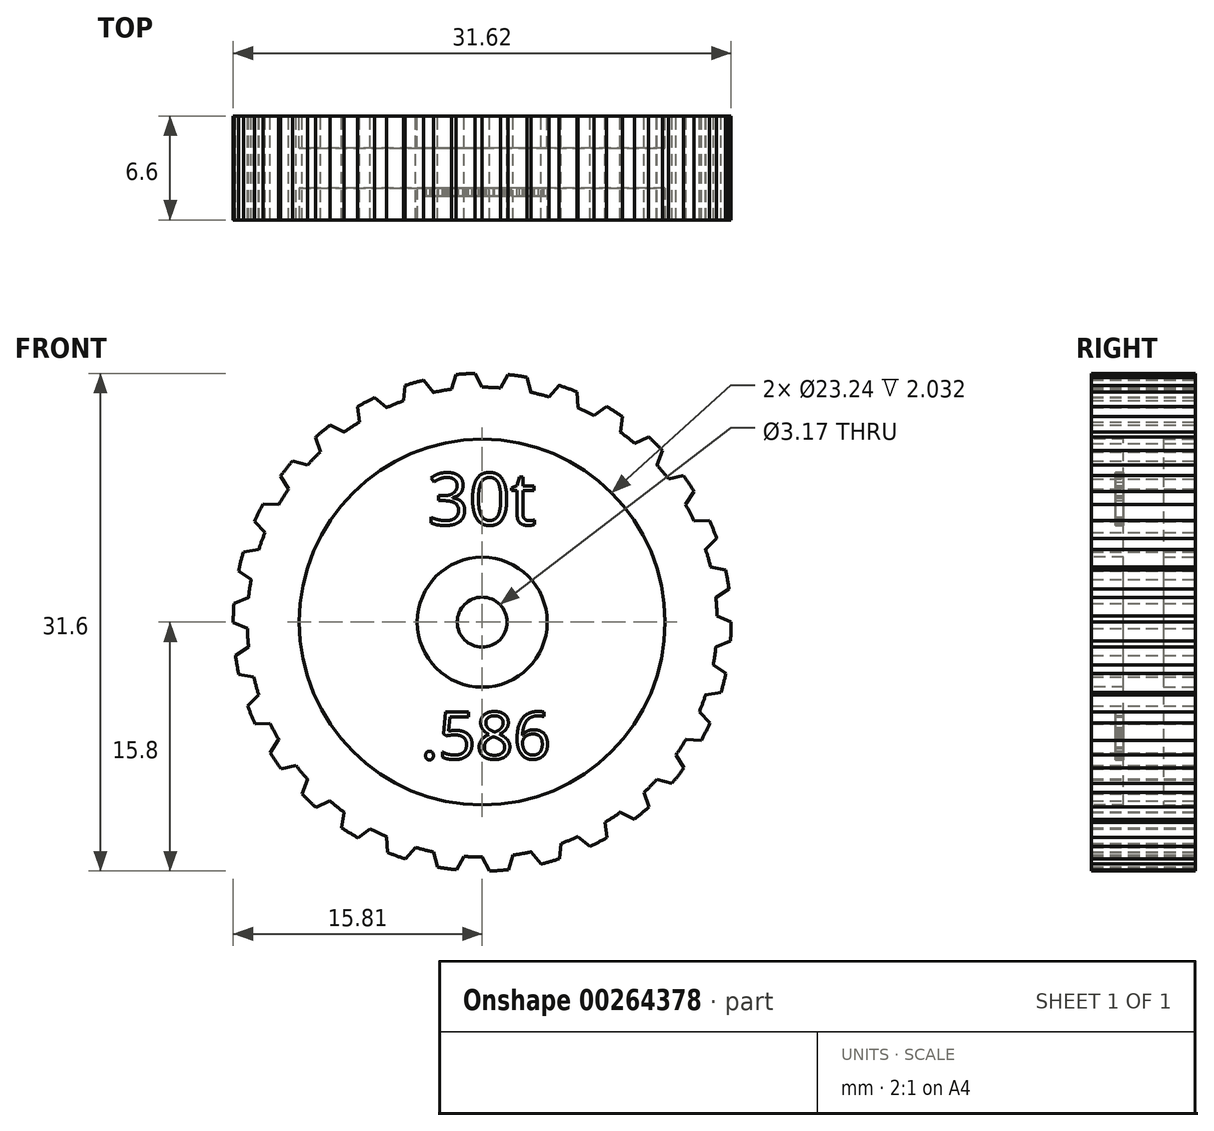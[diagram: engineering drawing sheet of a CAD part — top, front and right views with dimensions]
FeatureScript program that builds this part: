
annotation { "Feature Type Name" : "Feature", "Feature Type Description" : "" }
export const myFeature = defineFeature(function(context is Context, id is Id, definition is map)
    precondition{}
    {
        {
            var Q0;
            Q0=qCreatedBy(makeId("Front.planeOp"),FACE);
            var sketch = newSketch(context, id + "F0", { "sketchPlane" : qUnion([Q0])});
            skCircle(sketch, "E0", {"center": v(0, 0) * mm, "radius": 14.92 * mm});
            skCircle(sketch, "E1", {"center": v(0, 0) * mm, "radius": 1.59 * mm});
            skSolve(sketch);
        }
        {
            var Q0;
            Q0=qSketchRegion(id+"F0",true);
            extrude(context, id + "F1", {"entities" : qUnion([Q0]), "depth" : 6.6 * mm});
        }
        {
            var Q0;
            Q0=makeQuery(id+"F1.opExtrude","CAP_FACE",FACE,{"disambiguationData":[OSD([sQuery(id+"F0.wireOp",EDGE,"E0"),sQuery(id+"F0.wireOp",EDGE,"E1")])],"isStart":false});
            var sketch = newSketch(context, id + "F2", { "sketchPlane" : qUnion([Q0])});
            skCircle(sketch, "E2.0", {"center": v(0, 0) * mm, "radius": 11.62 * mm});
            skCircle(sketch, "E3", {"center": v(0, 0) * mm, "radius": 4.13 * mm});
            skSolve(sketch);
        }
        {
            var Q0;
            Q0=qSketchRegion(id+"F2",true);
            extrude(context, id + "F3", {"entities" : qUnion([Q0]), "operationType" : NewBodyOperationType.REMOVE, "oppositeDirection" : true, "depth" : 2.03 * mm});
        }
        {
            var Q0;
            Q0=makeQuery(id+"F1.opExtrude","CAP_FACE",FACE,{"disambiguationData":[OSD([sQuery(id+"F0.wireOp",EDGE,"E0"),sQuery(id+"F0.wireOp",EDGE,"E1")])],"isStart":true});
            var sketch = newSketch(context, id + "F4", { "sketchPlane" : qUnion([Q0])});
            skCircle(sketch, "E4.0", {"center": v(0, 0) * mm, "radius": 11.62 * mm});
            skCircle(sketch, "E5", {"center": v(0, 0) * mm, "radius": 4.13 * mm});
            skSolve(sketch);
        }
        {
            var Q0;
            Q0=qSketchRegion(id+"F4",true);
            extrude(context, id + "F5", {"entities" : qUnion([Q0]), "operationType" : NewBodyOperationType.REMOVE, "oppositeDirection" : true, "depth" : 2.03 * mm});
        }
        {
            var Q0;
            Q0=qCreatedBy(makeId("Front.planeOp"),FACE);
            var sketch = newSketch(context, id + "F6", { "sketchPlane" : qUnion([Q0])});
            skLineSegment(sketch, "E6", {"start": v(0, 0) * mm, "end": v(0, 18.01) * mm, "construction": true});
            skLineSegment(sketch, "E7", {"start": v(0, 0) * mm, "end": v(-3.72, 17.5) * mm, "construction": true});
            skLineSegment(sketch, "E8", {"start": v(0, 0) * mm, "end": v(-1.9, 18.03) * mm, "construction": true});
            skArc(sketch, "E9", {"start": v(-0.45, 15.8) * mm, "mid": v(-1.07, 15.78) * mm, "end": v(-1.68, 15.72) * mm});
            skLineSegment(sketch, "E10", {"start": v(0, 14.93) * mm, "end": v(-0.45, 15.8) * mm});
            skLineSegment(sketch, "E11", {"start": v(-1.68, 15.72) * mm, "end": v(-1.98, 14.7) * mm});
            skLineSegment(sketch, "E12", {"start": v(-1.98, 14.7) * mm, "end": v(0, 14.93) * mm});
            skLineSegment(sketch, "E13.1.0", {"start": v(-4.91, 15.03) * mm, "end": v(-5, 13.97) * mm});
            skArc(sketch, "E13.1.1", {"start": v(-3.73, 15.37) * mm, "mid": v(-4.32, 15.2) * mm, "end": v(-4.91, 15.03) * mm});
            skLineSegment(sketch, "E13.1.2", {"start": v(-3.1, 14.6) * mm, "end": v(-3.73, 15.37) * mm});
            skLineSegment(sketch, "E13.1.3", {"start": v(-5, 13.97) * mm, "end": v(-3.1, 14.6) * mm});
            skLineSegment(sketch, "E13.2.0", {"start": v(-7.93, 13.68) * mm, "end": v(-7.8, 12.62) * mm});
            skArc(sketch, "E13.2.1", {"start": v(-6.84, 14.25) * mm, "mid": v(-7.4, 13.98) * mm, "end": v(-7.93, 13.68) * mm});
            skLineSegment(sketch, "E13.2.2", {"start": v(-6.07, 13.64) * mm, "end": v(-6.84, 14.25) * mm});
            skLineSegment(sketch, "E13.2.3", {"start": v(-7.8, 12.62) * mm, "end": v(-6.07, 13.64) * mm});
            skLineSegment(sketch, "E13.3.0", {"start": v(-10.6, 11.73) * mm, "end": v(-10.25, 10.73) * mm});
            skArc(sketch, "E13.3.1", {"start": v(-9.66, 12.52) * mm, "mid": v(-10.14, 12.14) * mm, "end": v(-10.6, 11.73) * mm});
            skLineSegment(sketch, "E13.3.2", {"start": v(-8.77, 12.08) * mm, "end": v(-9.66, 12.52) * mm});
            skLineSegment(sketch, "E13.3.3", {"start": v(-10.25, 10.73) * mm, "end": v(-8.77, 12.08) * mm});
            skLineSegment(sketch, "E13.4.0", {"start": v(-12.8, 9.27) * mm, "end": v(-12.25, 8.36) * mm});
            skArc(sketch, "E13.4.1", {"start": v(-12.05, 10.24) * mm, "mid": v(-12.44, 9.76) * mm, "end": v(-12.8, 9.27) * mm});
            skLineSegment(sketch, "E13.4.2", {"start": v(-11.1, 9.99) * mm, "end": v(-12.05, 10.24) * mm});
            skLineSegment(sketch, "E13.4.3", {"start": v(-12.25, 8.36) * mm, "end": v(-11.1, 9.99) * mm});
            skLineSegment(sketch, "E13.5.0", {"start": v(-14.45, 6.4) * mm, "end": v(-13.72, 5.63) * mm});
            skArc(sketch, "E13.5.1", {"start": v(-13.91, 7.5) * mm, "mid": v(-14.2, 6.96) * mm, "end": v(-14.45, 6.4) * mm});
            skLineSegment(sketch, "E13.5.2", {"start": v(-12.93, 7.46) * mm, "end": v(-13.91, 7.5) * mm});
            skLineSegment(sketch, "E13.5.3", {"start": v(-13.72, 5.63) * mm, "end": v(-12.93, 7.46) * mm});
            skLineSegment(sketch, "E13.6.0", {"start": v(-15.47, 3.26) * mm, "end": v(-14.6, 2.65) * mm});
            skArc(sketch, "E13.6.1", {"start": v(-15.17, 4.45) * mm, "mid": v(-15.33, 3.86) * mm, "end": v(-15.47, 3.26) * mm});
            skLineSegment(sketch, "E13.6.2", {"start": v(-14.2, 4.61) * mm, "end": v(-15.17, 4.45) * mm});
            skLineSegment(sketch, "E13.6.3", {"start": v(-14.6, 2.65) * mm, "end": v(-14.2, 4.61) * mm});
            skLineSegment(sketch, "E13.7.0", {"start": v(-15.81, -0.03) * mm, "end": v(-14.83, -0.44) * mm});
            skArc(sketch, "E13.7.1", {"start": v(-15.77, 1.2) * mm, "mid": v(-15.8, 0.59) * mm, "end": v(-15.81, -0.03) * mm});
            skLineSegment(sketch, "E13.7.2", {"start": v(-14.84, 1.56) * mm, "end": v(-15.77, 1.2) * mm});
            skLineSegment(sketch, "E13.7.3", {"start": v(-14.83, -0.44) * mm, "end": v(-14.84, 1.56) * mm});
            skLineSegment(sketch, "E13.8.0", {"start": v(-15.46, -3.31) * mm, "end": v(-14.41, -3.51) * mm});
            skArc(sketch, "E13.8.1", {"start": v(-15.67, -2.1) * mm, "mid": v(-15.58, -2.7) * mm, "end": v(-15.46, -3.31) * mm});
            skLineSegment(sketch, "E13.8.2", {"start": v(-14.84, -1.56) * mm, "end": v(-15.67, -2.1) * mm});
            skLineSegment(sketch, "E13.8.3", {"start": v(-14.41, -3.51) * mm, "end": v(-14.84, -1.56) * mm});
            skLineSegment(sketch, "E13.9.0", {"start": v(-14.43, -6.45) * mm, "end": v(-13.37, -6.43) * mm});
            skArc(sketch, "E13.9.1", {"start": v(-14.9, -5.32) * mm, "mid": v(-14.67, -5.89) * mm, "end": v(-14.43, -6.45) * mm});
            skLineSegment(sketch, "E13.9.2", {"start": v(-14.2, -4.61) * mm, "end": v(-14.9, -5.32) * mm});
            skLineSegment(sketch, "E13.9.3", {"start": v(-13.37, -6.43) * mm, "end": v(-14.2, -4.61) * mm});
            skLineSegment(sketch, "E13.10.0", {"start": v(-12.78, -9.31) * mm, "end": v(-11.74, -9.07) * mm});
            skArc(sketch, "E13.10.1", {"start": v(-13.46, -8.3) * mm, "mid": v(-13.13, -8.81) * mm, "end": v(-12.78, -9.31) * mm});
            skLineSegment(sketch, "E13.10.2", {"start": v(-12.93, -7.46) * mm, "end": v(-13.46, -8.3) * mm});
            skLineSegment(sketch, "E13.10.3", {"start": v(-11.74, -9.07) * mm, "end": v(-12.93, -7.46) * mm});
            skLineSegment(sketch, "E13.11.0", {"start": v(-10.56, -11.77) * mm, "end": v(-9.6, -11.31) * mm});
            skArc(sketch, "E13.11.1", {"start": v(-11.44, -10.91) * mm, "mid": v(-11, -11.35) * mm, "end": v(-10.56, -11.77) * mm});
            skLineSegment(sketch, "E13.11.2", {"start": v(-11.1, -9.99) * mm, "end": v(-11.44, -10.91) * mm});
            skLineSegment(sketch, "E13.11.3", {"start": v(-9.6, -11.31) * mm, "end": v(-11.1, -9.99) * mm});
            skLineSegment(sketch, "E13.12.0", {"start": v(-7.88, -13.7) * mm, "end": v(-7.03, -13.06) * mm});
            skArc(sketch, "E13.12.1", {"start": v(-8.92, -13.05) * mm, "mid": v(-8.4, -13.39) * mm, "end": v(-7.88, -13.7) * mm});
            skLineSegment(sketch, "E13.12.2", {"start": v(-8.77, -12.08) * mm, "end": v(-8.92, -13.05) * mm});
            skLineSegment(sketch, "E13.12.3", {"start": v(-7.03, -13.06) * mm, "end": v(-8.77, -12.08) * mm});
            skLineSegment(sketch, "E13.13.0", {"start": v(-4.86, -15.05) * mm, "end": v(-4.17, -14.24) * mm});
            skArc(sketch, "E13.13.1", {"start": v(-6.01, -14.62) * mm, "mid": v(-5.44, -14.85) * mm, "end": v(-4.86, -15.05) * mm});
            skLineSegment(sketch, "E13.13.2", {"start": v(-6.07, -13.64) * mm, "end": v(-6.01, -14.62) * mm});
            skLineSegment(sketch, "E13.13.3", {"start": v(-4.17, -14.24) * mm, "end": v(-6.07, -13.64) * mm});
            skLineSegment(sketch, "E13.14.0", {"start": v(-1.63, -15.73) * mm, "end": v(-1.11, -14.8) * mm});
            skArc(sketch, "E13.14.1", {"start": v(-2.84, -15.55) * mm, "mid": v(-2.24, -15.65) * mm, "end": v(-1.63, -15.73) * mm});
            skLineSegment(sketch, "E13.14.2", {"start": v(-3.1, -14.6) * mm, "end": v(-2.84, -15.55) * mm});
            skLineSegment(sketch, "E13.14.3", {"start": v(-1.11, -14.8) * mm, "end": v(-3.1, -14.6) * mm});
            skLineSegment(sketch, "E13.15.0", {"start": v(1.68, -15.72) * mm, "end": v(1.98, -14.7) * mm});
            skArc(sketch, "E13.15.1", {"start": v(0.45, -15.8) * mm, "mid": v(1.07, -15.78) * mm, "end": v(1.68, -15.72) * mm});
            skLineSegment(sketch, "E13.15.2", {"start": v(0, -14.93) * mm, "end": v(0.45, -15.8) * mm});
            skLineSegment(sketch, "E13.15.3", {"start": v(1.98, -14.7) * mm, "end": v(0, -14.93) * mm});
            skLineSegment(sketch, "E13.16.0", {"start": v(4.91, -15.03) * mm, "end": v(5, -13.97) * mm});
            skArc(sketch, "E13.16.1", {"start": v(3.73, -15.37) * mm, "mid": v(4.32, -15.2) * mm, "end": v(4.91, -15.03) * mm});
            skLineSegment(sketch, "E13.16.2", {"start": v(3.1, -14.6) * mm, "end": v(3.73, -15.37) * mm});
            skLineSegment(sketch, "E13.16.3", {"start": v(5, -13.97) * mm, "end": v(3.1, -14.6) * mm});
            skLineSegment(sketch, "E13.17.0", {"start": v(7.93, -13.68) * mm, "end": v(7.8, -12.62) * mm});
            skArc(sketch, "E13.17.1", {"start": v(6.84, -14.25) * mm, "mid": v(7.4, -13.98) * mm, "end": v(7.93, -13.68) * mm});
            skLineSegment(sketch, "E13.17.2", {"start": v(6.07, -13.64) * mm, "end": v(6.84, -14.25) * mm});
            skLineSegment(sketch, "E13.17.3", {"start": v(7.8, -12.62) * mm, "end": v(6.07, -13.64) * mm});
            skLineSegment(sketch, "E13.18.0", {"start": v(10.6, -11.73) * mm, "end": v(10.25, -10.73) * mm});
            skArc(sketch, "E13.18.1", {"start": v(9.66, -12.52) * mm, "mid": v(10.14, -12.14) * mm, "end": v(10.6, -11.73) * mm});
            skLineSegment(sketch, "E13.18.2", {"start": v(8.77, -12.08) * mm, "end": v(9.66, -12.52) * mm});
            skLineSegment(sketch, "E13.18.3", {"start": v(10.25, -10.73) * mm, "end": v(8.77, -12.08) * mm});
            skLineSegment(sketch, "E13.19.0", {"start": v(12.8, -9.27) * mm, "end": v(12.25, -8.36) * mm});
            skArc(sketch, "E13.19.1", {"start": v(12.05, -10.24) * mm, "mid": v(12.44, -9.76) * mm, "end": v(12.8, -9.27) * mm});
            skLineSegment(sketch, "E13.19.2", {"start": v(11.1, -9.99) * mm, "end": v(12.05, -10.24) * mm});
            skLineSegment(sketch, "E13.19.3", {"start": v(12.25, -8.36) * mm, "end": v(11.1, -9.99) * mm});
            skLineSegment(sketch, "E13.20.0", {"start": v(14.45, -6.4) * mm, "end": v(13.72, -5.63) * mm});
            skArc(sketch, "E13.20.1", {"start": v(13.91, -7.5) * mm, "mid": v(14.2, -6.96) * mm, "end": v(14.45, -6.4) * mm});
            skLineSegment(sketch, "E13.20.2", {"start": v(12.93, -7.46) * mm, "end": v(13.91, -7.5) * mm});
            skLineSegment(sketch, "E13.20.3", {"start": v(13.72, -5.63) * mm, "end": v(12.93, -7.46) * mm});
            skLineSegment(sketch, "E13.21.0", {"start": v(15.47, -3.26) * mm, "end": v(14.6, -2.65) * mm});
            skArc(sketch, "E13.21.1", {"start": v(15.17, -4.45) * mm, "mid": v(15.33, -3.86) * mm, "end": v(15.47, -3.26) * mm});
            skLineSegment(sketch, "E13.21.2", {"start": v(14.2, -4.61) * mm, "end": v(15.17, -4.45) * mm});
            skLineSegment(sketch, "E13.21.3", {"start": v(14.6, -2.65) * mm, "end": v(14.2, -4.61) * mm});
            skLineSegment(sketch, "E13.22.0", {"start": v(15.81, 0.03) * mm, "end": v(14.83, 0.44) * mm});
            skArc(sketch, "E13.22.1", {"start": v(15.77, -1.2) * mm, "mid": v(15.8, -0.59) * mm, "end": v(15.81, 0.03) * mm});
            skLineSegment(sketch, "E13.22.2", {"start": v(14.84, -1.56) * mm, "end": v(15.77, -1.2) * mm});
            skLineSegment(sketch, "E13.22.3", {"start": v(14.83, 0.44) * mm, "end": v(14.84, -1.56) * mm});
            skLineSegment(sketch, "E13.23.0", {"start": v(15.46, 3.31) * mm, "end": v(14.41, 3.51) * mm});
            skArc(sketch, "E13.23.1", {"start": v(15.67, 2.1) * mm, "mid": v(15.58, 2.7) * mm, "end": v(15.46, 3.31) * mm});
            skLineSegment(sketch, "E13.23.2", {"start": v(14.84, 1.56) * mm, "end": v(15.67, 2.1) * mm});
            skLineSegment(sketch, "E13.23.3", {"start": v(14.41, 3.51) * mm, "end": v(14.84, 1.56) * mm});
            skLineSegment(sketch, "E13.24.0", {"start": v(14.43, 6.45) * mm, "end": v(13.37, 6.43) * mm});
            skArc(sketch, "E13.24.1", {"start": v(14.9, 5.32) * mm, "mid": v(14.67, 5.89) * mm, "end": v(14.43, 6.45) * mm});
            skLineSegment(sketch, "E13.24.2", {"start": v(14.2, 4.61) * mm, "end": v(14.9, 5.32) * mm});
            skLineSegment(sketch, "E13.24.3", {"start": v(13.37, 6.43) * mm, "end": v(14.2, 4.61) * mm});
            skLineSegment(sketch, "E13.25.0", {"start": v(12.78, 9.31) * mm, "end": v(11.74, 9.07) * mm});
            skArc(sketch, "E13.25.1", {"start": v(13.46, 8.3) * mm, "mid": v(13.13, 8.81) * mm, "end": v(12.78, 9.31) * mm});
            skLineSegment(sketch, "E13.25.2", {"start": v(12.93, 7.46) * mm, "end": v(13.46, 8.3) * mm});
            skLineSegment(sketch, "E13.25.3", {"start": v(11.74, 9.07) * mm, "end": v(12.93, 7.46) * mm});
            skLineSegment(sketch, "E13.26.0", {"start": v(10.56, 11.77) * mm, "end": v(9.6, 11.31) * mm});
            skArc(sketch, "E13.26.1", {"start": v(11.44, 10.91) * mm, "mid": v(11, 11.35) * mm, "end": v(10.56, 11.77) * mm});
            skLineSegment(sketch, "E13.26.2", {"start": v(11.1, 9.99) * mm, "end": v(11.44, 10.91) * mm});
            skLineSegment(sketch, "E13.26.3", {"start": v(9.6, 11.31) * mm, "end": v(11.1, 9.99) * mm});
            skLineSegment(sketch, "E13.27.0", {"start": v(7.88, 13.7) * mm, "end": v(7.03, 13.06) * mm});
            skArc(sketch, "E13.27.1", {"start": v(8.92, 13.05) * mm, "mid": v(8.4, 13.39) * mm, "end": v(7.88, 13.7) * mm});
            skLineSegment(sketch, "E13.27.2", {"start": v(8.77, 12.08) * mm, "end": v(8.92, 13.05) * mm});
            skLineSegment(sketch, "E13.27.3", {"start": v(7.03, 13.06) * mm, "end": v(8.77, 12.08) * mm});
            skLineSegment(sketch, "E13.28.0", {"start": v(4.86, 15.05) * mm, "end": v(4.17, 14.24) * mm});
            skArc(sketch, "E13.28.1", {"start": v(6.01, 14.62) * mm, "mid": v(5.44, 14.85) * mm, "end": v(4.86, 15.05) * mm});
            skLineSegment(sketch, "E13.28.2", {"start": v(6.07, 13.64) * mm, "end": v(6.01, 14.62) * mm});
            skLineSegment(sketch, "E13.28.3", {"start": v(4.17, 14.24) * mm, "end": v(6.07, 13.64) * mm});
            skLineSegment(sketch, "E13.29.0", {"start": v(1.63, 15.73) * mm, "end": v(1.11, 14.8) * mm});
            skArc(sketch, "E13.29.1", {"start": v(2.84, 15.55) * mm, "mid": v(2.24, 15.65) * mm, "end": v(1.63, 15.73) * mm});
            skLineSegment(sketch, "E13.29.2", {"start": v(3.1, 14.6) * mm, "end": v(2.84, 15.55) * mm});
            skLineSegment(sketch, "E13.29.3", {"start": v(1.11, 14.8) * mm, "end": v(3.1, 14.6) * mm});
            skSolve(sketch);
        }
        {
            var Q0;
            Q0=qSketchRegion(id+"F6",true);
            var Q1;
            {var subQ0=sQuery(id+"F0.wireOp",EDGE,"E0");Q1=makeQuery(id+"F3.boolean.opBoolean","SPLIT",FACE,{"disambiguationData":[TD([makeQuery(id+"F1.opExtrude","SWEPT_FACE",FACE,{"disambiguationData":[OSD([subQ0])]})])],"derivedFrom":makeQuery(id+"F1.opExtrude","CAP_FACE",FACE,{"disambiguationData":[OSD([subQ0,sQuery(id+"F0.wireOp",EDGE,"E1")])],"isStart":false})});}
            extrude(context, id + "F7", {"entities" : qUnion([Q0]), "operationType" : NewBodyOperationType.ADD, "endBound" : BoundingType.UP_TO_SURFACE, "endBoundEntityFace" : qUnion([Q1]), "depth" : 25.4 * mm});
        }
        {
            var Q0;
            Q0=makeQuery(id+"F3.boolean.opBoolean","COPY",FACE,{"derivedFrom":makeQuery(id+"F3.opExtrude","CAP_FACE",FACE,{"disambiguationData":[OSD([sQuery(id+"F2.wireOp",EDGE,"E2.0"),sQuery(id+"F2.wireOp",EDGE,"E3")])],"isStart":false})});
            var sketch = newSketch(context, id + "F8", { "sketchPlane" : qUnion([Q0])});
            skText(sketch, "E14", { "text": "30t", "fontName": "OpenSans-Regular.ttf"});
            skText(sketch, "E15", { "text": ".586", "fontName": "OpenSans-Regular.ttf"});
            const initialGuessF8  = {"E14": [-0.00347, 0.00618, 1, 0, 0.00331], "E15": [-0.0039, -0.00869, 1, 0, 0.003]};
            skSetInitialGuess(sketch, initialGuessF8);
            skSolve(sketch);
        }
        {
            var Q0;
            Q0=qSketchRegion(id+"F8",true);
            extrude(context, id + "F9", {"entities" : qUnion([Q0]), "operationType" : NewBodyOperationType.ADD, "depth" : 0.5 * mm});
        }
    });
